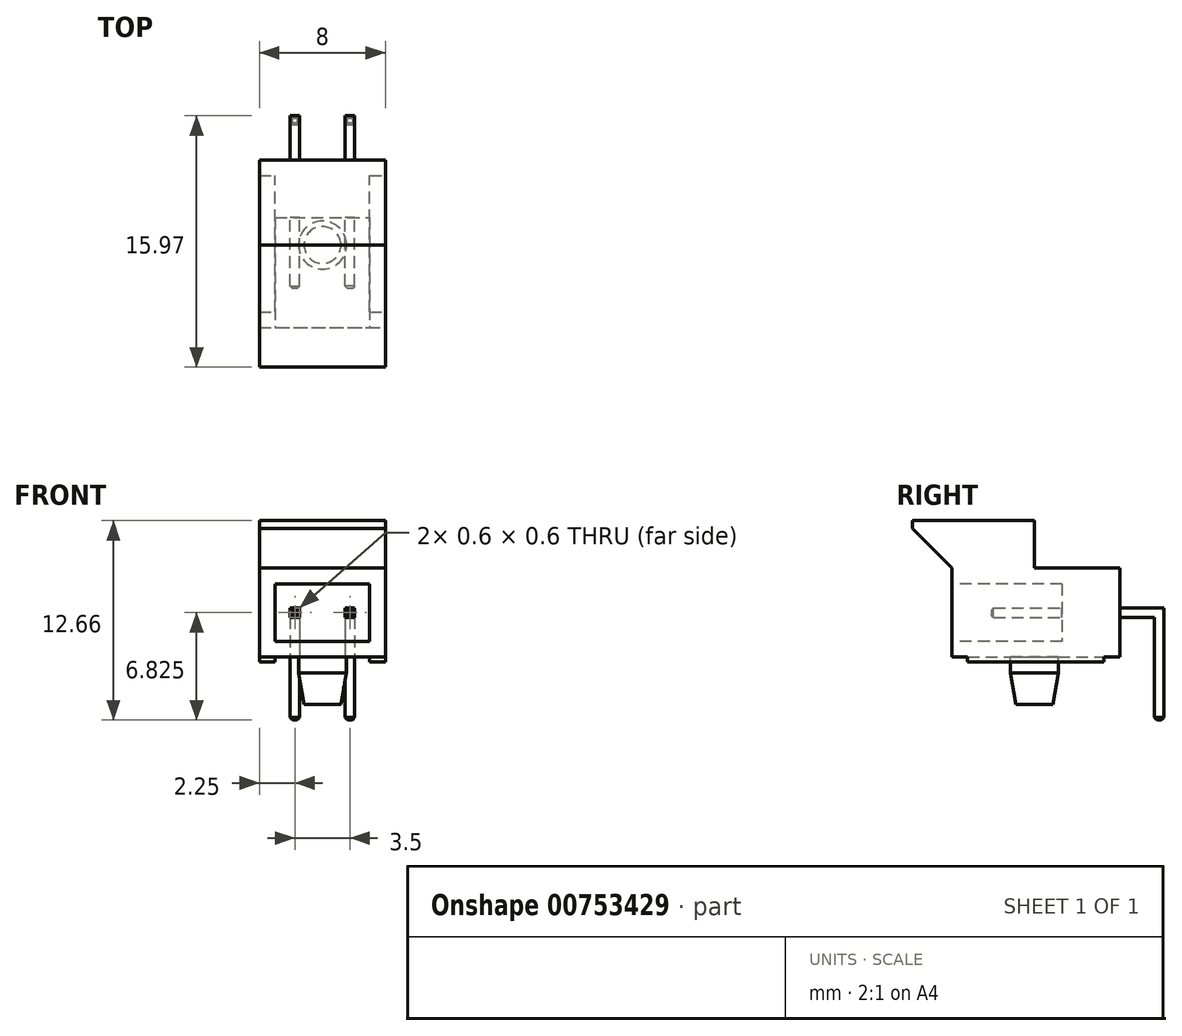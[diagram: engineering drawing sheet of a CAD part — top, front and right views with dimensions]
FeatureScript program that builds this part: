
annotation { "Feature Type Name" : "Feature", "Feature Type Description" : "" }
export const myFeature = defineFeature(function(context is Context, id is Id, definition is map)
    precondition{}
    {
        {
            var Q0;
            Q0=qCreatedBy(makeId("Top.planeOp"),FACE);
            var sketch = newSketch(context, id + "F0", { "sketchPlane" : qUnion([Q0])});
            skLineSegment(sketch, "E0.bottom", {"start": v(-4, 7.83) * mm, "end": v(4, 7.83) * mm});
            skLineSegment(sketch, "E0.top", {"start": v(-4, -7.83) * mm, "end": v(4, -7.83) * mm});
            skLineSegment(sketch, "E0.left", {"start": v(-4, 7.83) * mm, "end": v(-4, -7.83) * mm});
            skLineSegment(sketch, "E0.right", {"start": v(4, 7.83) * mm, "end": v(4, -7.83) * mm});
            skCircle(sketch, "E1", {"center": v(0, -2.58) * mm, "radius": 1.52 * mm});
            skCircle(sketch, "E2", {"center": v(-1.75, 5.33) * mm, "radius": 0.51 * mm});
            skCircle(sketch, "E3", {"center": v(0, 5.33) * mm, "radius": 0.51 * mm, "construction": true});
            skCircle(sketch, "E4", {"center": v(1.75, 5.33) * mm, "radius": 0.51 * mm});
            skLineSegment(sketch, "E5", {"start": v(-4, 2.83) * mm, "end": v(4, 2.83) * mm});
            skSolve(sketch);
        }
        {
            var Q0;
            {var subQ1=sQuery(id+"F0.wireOp",EDGE,"E0.top");Q0=makeQuery(id+"F0.imprint","IMPRINT",FACE,{"disambiguationData":[TD([[makeQuery(id+"F0.imprint","IMPRINT",EDGE,{"derivedFrom":subQ1}),1.0]])]});}
            var Q1;
            Q1=makeQuery(id+"F0.imprint","IMPRINT",FACE,{"disambiguationData":[TD([[makeQuery(id+"F0.imprint","IMPRINT",EDGE,{"derivedFrom":sQuery(id+"F0.wireOp",EDGE,"E1")}),1.0]])]});
            extrude(context, id + "F1", {"entities" : qUnion([Q0, Q1]), "depth" : 5.65 * mm, "offsetDistance" : 25 * mm});
        }
        {
            var Q0;
            Q0=makeQuery(id+"F0.imprint","IMPRINT",FACE,{"disambiguationData":[TD([[makeQuery(id+"F0.imprint","IMPRINT",EDGE,{"derivedFrom":sQuery(id+"F0.wireOp",EDGE,"E1")}),1.0]])]});
            extrude(context, id + "F2", {"entities" : qUnion([Q0]), "operationType" : NewBodyOperationType.ADD, "oppositeDirection" : true, "depth" : 3 * mm, "offsetDistance" : 25 * mm});
        }
        {
            var Q0;
            Q0=makeQuery(id+"F2.opExtrude","CAP_EDGE",EDGE,{"disambiguationData":[OSD([sQuery(id+"F0.wireOp",EDGE,"E1")])],"isStart":false});
            chamfer(context, id + "F3", {"entities" : qUnion([Q0]), "chamferType" : ChamferType.OFFSET_ANGLE, "width" : 2 * mm, "oppositeDirection" : false, "angle" : 10 * degree, "tangentPropagation" : true});
        }
        {
            var Q0;
            Q0=makeQuery(id+"F1.opExtrude","SWEPT_FACE",FACE,{"disambiguationData":[OSD([sQuery(id+"F0.wireOp",EDGE,"E0.top")])]});
            var sketch = newSketch(context, id + "F4", { "sketchPlane" : qUnion([Q0])});
            skLineSegment(sketch, "E6.bottom", {"start": v(-3, 4.65) * mm, "end": v(3, 4.65) * mm});
            skLineSegment(sketch, "E6.top", {"start": v(-3, 1) * mm, "end": v(3, 1) * mm});
            skLineSegment(sketch, "E6.left", {"start": v(-3, 4.65) * mm, "end": v(-3, 1) * mm});
            skLineSegment(sketch, "E6.right", {"start": v(3, 4.65) * mm, "end": v(3, 1) * mm});
            skSolve(sketch);
        }
        {
            var Q0;
            Q0=makeQuery(id+"F4.imprint","IMPRINT",FACE,{"disambiguationData":[TD([[makeQuery(id+"F4.imprint","IMPRINT",EDGE,{"derivedFrom":sQuery(id+"F4.wireOp",EDGE,"E6.bottom")}),-1.0]])]});
            extrude(context, id + "F5", {"entities" : qUnion([Q0]), "operationType" : NewBodyOperationType.REMOVE, "oppositeDirection" : true, "depth" : 7 * mm, "offsetDistance" : 25 * mm});
        }
        {
            var Q0;
            Q0=makeQuery(id+"F1.opExtrude","SWEPT_FACE",FACE,{"disambiguationData":[OSD([sQuery(id+"F0.wireOp",EDGE,"E0.right")])]});
            var Q1;
            Q1=makeQuery(id+"F1.opExtrude","SWEPT_FACE",FACE,{"disambiguationData":[OSD([sQuery(id+"F0.wireOp",EDGE,"E0.left")])]});
            cPlane(context, id + "F6", {"entities" : qUnion([Q0, Q1]), "cplaneType" : CPlaneType.MID_PLANE, "offset" : 25 * mm, "width" : 150 * mm, "height" : 150 * mm});
        }
        {
            var Q0;
            Q0=qCreatedBy(id+"F6.planeOp",FACE);
            var sketch = newSketch(context, id + "F7", { "sketchPlane" : qUnion([Q0])});
            skLineSegment(sketch, "E7.bottom", {"start": v(-5.33, 3.12) * mm, "end": v(5.63, 3.12) * mm});
            skLineSegment(sketch, "E7.top", {"start": v(-5.33, 2.53) * mm, "end": v(5.63, 2.53) * mm});
            skLineSegment(sketch, "E7.left", {"start": v(-5.33, 3.12) * mm, "end": v(-5.33, 2.53) * mm});
            skLineSegment(sketch, "E7.right", {"start": v(5.63, 3.12) * mm, "end": v(5.63, 2.53) * mm});
            skLineSegment(sketch, "E8.bottom", {"start": v(5.63, 3.12) * mm, "end": v(5.03, 3.12) * mm});
            skLineSegment(sketch, "E8.top", {"start": v(5.63, -4) * mm, "end": v(5.03, -4) * mm});
            skLineSegment(sketch, "E8.left", {"start": v(5.63, 3.12) * mm, "end": v(5.63, -4) * mm});
            skLineSegment(sketch, "E8.right", {"start": v(5.03, 3.12) * mm, "end": v(5.03, -4) * mm});
            skLineSegment(sketch, "E9.0", {"start": v(4.82, 0) * mm, "end": v(5.84, 0) * mm});
            skLineSegment(sketch, "E10.0.0", {"start": v(-7.83, 4.65) * mm, "end": v(-7.83, 1) * mm});
            skLineSegment(sketch, "E10.0.1", {"start": v(-7.83, 1) * mm, "end": v(-0.83, 1) * mm});
            skLineSegment(sketch, "E10.0.2", {"start": v(-0.83, 1) * mm, "end": v(-0.83, 4.65) * mm});
            skLineSegment(sketch, "E10.0.3", {"start": v(-0.83, 4.65) * mm, "end": v(-7.83, 4.65) * mm});
            skLineSegment(sketch, "E11", {"start": v(-5.33, 2.83) * mm, "end": v(5.63, 2.83) * mm, "construction": true});
            skLineSegment(sketch, "E12", {"start": v(5.33, 3.12) * mm, "end": v(5.33, -4) * mm, "construction": true});
            skSolve(sketch);
        }
        {
            var Q0;
            Q0=qCreatedBy(id+"F6.planeOp",FACE);
            cPlane(context, id + "F8", {"entities" : qUnion([Q0]), "cplaneType" : CPlaneType.OFFSET, "offset" : 1.75 * mm, "width" : 150 * mm, "height" : 150 * mm});
        }
        {
            var Q0;
            Q0=qCreatedBy(id+"F8.planeOp",FACE);
            var sketch = newSketch(context, id + "F9", { "sketchPlane" : qUnion([Q0])});
            skLineSegment(sketch, "E13.0", {"start": v(-5.33, 3.12) * mm, "end": v(5.63, 3.12) * mm});
            skLineSegment(sketch, "E14.0", {"start": v(-5.33, 2.53) * mm, "end": v(5.63, 2.53) * mm});
            skLineSegment(sketch, "E15.0", {"start": v(-5.33, 3.12) * mm, "end": v(-5.33, 2.53) * mm});
            skLineSegment(sketch, "E16.0", {"start": v(5.63, 3.12) * mm, "end": v(5.63, -4) * mm});
            skLineSegment(sketch, "E17.0", {"start": v(5.03, 3.12) * mm, "end": v(5.03, -4) * mm});
            skLineSegment(sketch, "E18.0", {"start": v(5.63, -4) * mm, "end": v(5.03, -4) * mm});
            skSolve(sketch);
        }
        {
            var Q0;
            Q0=qCreatedBy(id+"F6.planeOp",FACE);
            cPlane(context, id + "F10", {"entities" : qUnion([Q0]), "cplaneType" : CPlaneType.OFFSET, "offset" : 1.75 * mm, "oppositeDirection" : true, "width" : 150 * mm, "height" : 150 * mm});
        }
        {
            var Q0;
            Q0=qCreatedBy(id+"F10.planeOp",FACE);
            var sketch = newSketch(context, id + "F11", { "sketchPlane" : qUnion([Q0])});
            skLineSegment(sketch, "E19.0", {"start": v(-5.33, 3.12) * mm, "end": v(5.63, 3.12) * mm});
            skLineSegment(sketch, "E20.0", {"start": v(5.63, 3.12) * mm, "end": v(5.63, -4) * mm});
            skLineSegment(sketch, "E21.0", {"start": v(5.63, -4) * mm, "end": v(5.03, -4) * mm});
            skLineSegment(sketch, "E22.0", {"start": v(5.03, 3.12) * mm, "end": v(5.03, -4) * mm});
            skLineSegment(sketch, "E23.0", {"start": v(-5.33, 2.53) * mm, "end": v(5.63, 2.53) * mm});
            skLineSegment(sketch, "E24.0", {"start": v(-5.33, 3.12) * mm, "end": v(-5.33, 2.53) * mm});
            skSolve(sketch);
        }
        {
            var Q0;
            Q0=makeQuery(id+"F1.opExtrude","CAP_FACE",FACE,{"disambiguationData":[OSD([sQuery(id+"F0.wireOp",EDGE,"E0.top"),sQuery(id+"F0.wireOp",EDGE,"E0.left"),sQuery(id+"F0.wireOp",EDGE,"E0.right"),sQuery(id+"F0.wireOp",EDGE,"E5")])],"isStart":true});
            var sketch = newSketch(context, id + "F12", { "sketchPlane" : qUnion([Q0])});
            skLineSegment(sketch, "E25.bottom", {"start": v(-4, 6.83) * mm, "end": v(-3, 6.83) * mm});
            skLineSegment(sketch, "E25.top", {"start": v(-4, -1.83) * mm, "end": v(-3, -1.83) * mm});
            skLineSegment(sketch, "E25.left", {"start": v(-4, 6.83) * mm, "end": v(-4, -1.83) * mm});
            skLineSegment(sketch, "E25.right", {"start": v(-3, 6.83) * mm, "end": v(-3, -1.83) * mm});
            skLineSegment(sketch, "E26.bottom", {"start": v(3, 6.83) * mm, "end": v(4, 6.83) * mm});
            skLineSegment(sketch, "E26.top", {"start": v(3, -1.83) * mm, "end": v(4, -1.83) * mm});
            skLineSegment(sketch, "E26.left", {"start": v(3, 6.83) * mm, "end": v(3, -1.83) * mm});
            skLineSegment(sketch, "E26.right", {"start": v(4, 6.83) * mm, "end": v(4, -1.83) * mm});
            skSolve(sketch);
        }
        {
            var Q0;
            Q0=makeQuery(id+"F12.imprint","IMPRINT",FACE,{"disambiguationData":[TD([[makeQuery(id+"F12.imprint","IMPRINT",EDGE,{"derivedFrom":sQuery(id+"F12.wireOp",EDGE,"E26.bottom")}),-1.0]])]});
            var Q1;
            Q1=makeQuery(id+"F12.imprint","IMPRINT",FACE,{"disambiguationData":[TD([[makeQuery(id+"F12.imprint","IMPRINT",EDGE,{"derivedFrom":sQuery(id+"F12.wireOp",EDGE,"E25.bottom")}),-1.0]])]});
            extrude(context, id + "F13", {"entities" : qUnion([Q0, Q1]), "operationType" : NewBodyOperationType.ADD, "depth" : 0.3 * mm, "offsetDistance" : 25 * mm});
        }
        {
            var Q0;
            Q0=makeQuery(id+"F13.boolean.opBoolean","MERGE",FACE,{"derivedFrom":[makeQuery(id+"F1.opExtrude","SWEPT_FACE",FACE,{"disambiguationData":[OSD([sQuery(id+"F0.wireOp",EDGE,"E0.right")])]}),makeQuery(id+"F13.opExtrude","SWEPT_FACE",FACE,{"disambiguationData":[OSD([sQuery(id+"F12.wireOp",EDGE,"E26.right")])]})]});
            var sketch = newSketch(context, id + "F14", { "sketchPlane" : qUnion([Q0])});
            skLineSegment(sketch, "E27", {"start": v(-7.83, 5.65) * mm, "end": v(-10.84, 8.66) * mm});
            skLineSegment(sketch, "E28", {"start": v(-10.84, 8.66) * mm, "end": v(-2.58, 8.66) * mm});
            skLineSegment(sketch, "E29", {"start": v(-2.58, 8.66) * mm, "end": v(-2.58, 5.65) * mm});
            skLineSegment(sketch, "E30.0", {"start": v(-1.4, -3) * mm, "end": v(-3.75, -3) * mm});
            skLineSegment(sketch, "E31", {"start": v(-10.34, 8.16) * mm, "end": v(-10.34, 8.66) * mm});
            skSolve(sketch);
        }
        {
            var Q0;
            {var subQ0=sQuery(id+"F14.wireOp",EDGE,"E29");Q0=makeQuery(id+"F14.imprint","IMPRINT",FACE,{"disambiguationData":[TD([[makeQuery(id+"F14.imprint","IMPRINT",EDGE,{"derivedFrom":subQ0}),-1.0]])]});}
            var Q1;
            Q1=makeQuery(id+"F13.boolean.opBoolean","MERGE",FACE,{"derivedFrom":[makeQuery(id+"F1.opExtrude","SWEPT_FACE",FACE,{"disambiguationData":[OSD([sQuery(id+"F0.wireOp",EDGE,"E0.left")])]}),makeQuery(id+"F13.opExtrude","SWEPT_FACE",FACE,{"disambiguationData":[OSD([sQuery(id+"F12.wireOp",EDGE,"E25.left")])]})]});
            extrude(context, id + "F15", {"entities" : qUnion([Q0]), "operationType" : NewBodyOperationType.ADD, "endBound" : BoundingType.UP_TO_SURFACE, "oppositeDirection" : true, "depth" : 25 * mm, "endBoundEntityFace" : qUnion([Q1]), "offsetDistance" : 25 * mm});
        }
        {
            var Q0;
            {var subQ5=sQuery(id+"F9.wireOp",EDGE,"E18.0");Q0=makeQuery(id+"F9.imprint","IMPRINT",FACE,{"disambiguationData":[TD([[makeQuery(id+"F9.imprint","IMPRINT",EDGE,{"derivedFrom":subQ5}),-1.0]])]});}
            var Q1;
            {var subQ0=sQuery(id+"F9.wireOp",EDGE,"E15.0");Q1=makeQuery(id+"F9.imprint","IMPRINT",FACE,{"disambiguationData":[TD([[makeQuery(id+"F9.imprint","IMPRINT",EDGE,{"derivedFrom":subQ0}),1.0]])]});}
            var Q2;
            {var subQ0=sQuery(id+"F9.wireOp",EDGE,"E16.0");var subQ1=sQuery(id+"F9.wireOp",EDGE,"E13.0");var subQ2=makeQuery(id+"F9.imprint","INTERSECT",VERTEX,{"derivedFrom":[subQ1,subQ0]});Q2=makeQuery(id+"F9.imprint","IMPRINT",FACE,{"disambiguationData":[TD([[makeQuery(id+"F9.imprint","IMPRINT",EDGE,{"disambiguationData":[TD([[subQ2,1.0]])],"derivedFrom":subQ1}),-1.0]])]});}
            var Q3;
            {var subQ0=sQuery(id+"F11.wireOp",EDGE,"E24.0");Q3=makeQuery(id+"F11.imprint","IMPRINT",FACE,{"disambiguationData":[TD([[makeQuery(id+"F11.imprint","IMPRINT",EDGE,{"derivedFrom":subQ0}),1.0]])]});}
            var Q4;
            {var subQ0=sQuery(id+"F11.wireOp",EDGE,"E20.0");var subQ1=sQuery(id+"F11.wireOp",EDGE,"E19.0");var subQ2=makeQuery(id+"F11.imprint","INTERSECT",VERTEX,{"derivedFrom":[subQ1,subQ0]});Q4=makeQuery(id+"F11.imprint","IMPRINT",FACE,{"disambiguationData":[TD([[makeQuery(id+"F11.imprint","IMPRINT",EDGE,{"disambiguationData":[TD([[subQ2,1.0]])],"derivedFrom":subQ1}),-1.0]])]});}
            var Q5;
            {var subQ0=sQuery(id+"F11.wireOp",EDGE,"E21.0");Q5=makeQuery(id+"F11.imprint","IMPRINT",FACE,{"disambiguationData":[TD([[makeQuery(id+"F11.imprint","IMPRINT",EDGE,{"derivedFrom":subQ0}),-1.0]])]});}
            extrude(context, id + "F16", {"entities" : qUnion([Q0, Q1, Q2, Q3, Q4, Q5]), "operationType" : NewBodyOperationType.ADD, "depth" : 0.3 * mm, "offsetDistance" : 25 * mm, "hasSecondDirection" : true, "secondDirectionOppositeDirection" : true, "secondDirectionDepth" : 0.3 * mm});
        }
        {
            var Q0;
            Q0=makeQuery(id+"F16.opExtrude","SWEPT_EDGE",EDGE,{"disambiguationData":[OSD([sQuery(id+"F11.wireOp",EDGE,"E19.0"),sQuery(id+"F11.wireOp",EDGE,"E24.0")])]});
            var Q1;
            Q1=makeQuery(id+"F16.opExtrude","SWEPT_EDGE",EDGE,{"disambiguationData":[OSD([sQuery(id+"F11.wireOp",EDGE,"E23.0"),sQuery(id+"F11.wireOp",EDGE,"E24.0")])]});
            var Q2;
            Q2=makeQuery(id+"F16.opExtrude","CAP_EDGE",EDGE,{"disambiguationData":[OSD([sQuery(id+"F11.wireOp",EDGE,"E24.0")])],"isStart":true});
            var Q3;
            Q3=makeQuery(id+"F16.opExtrude","CAP_EDGE",EDGE,{"disambiguationData":[OSD([sQuery(id+"F11.wireOp",EDGE,"E24.0")])],"isStart":false});
            var Q4;
            Q4=makeQuery(id+"F16.opExtrude","SWEPT_EDGE",EDGE,{"disambiguationData":[OSD([sQuery(id+"F9.wireOp",EDGE,"E13.0"),sQuery(id+"F9.wireOp",EDGE,"E15.0")])]});
            var Q5;
            Q5=makeQuery(id+"F16.opExtrude","CAP_EDGE",EDGE,{"disambiguationData":[OSD([sQuery(id+"F9.wireOp",EDGE,"E15.0")])],"isStart":true});
            var Q6;
            Q6=makeQuery(id+"F16.opExtrude","SWEPT_EDGE",EDGE,{"disambiguationData":[OSD([sQuery(id+"F9.wireOp",EDGE,"E14.0"),sQuery(id+"F9.wireOp",EDGE,"E15.0")])]});
            var Q7;
            Q7=makeQuery(id+"F16.opExtrude","CAP_EDGE",EDGE,{"disambiguationData":[OSD([sQuery(id+"F9.wireOp",EDGE,"E15.0")])],"isStart":false});
            var Q8;
            Q8=makeQuery(id+"F16.opExtrude","SWEPT_EDGE",EDGE,{"disambiguationData":[OSD([sQuery(id+"F9.wireOp",EDGE,"E16.0"),sQuery(id+"F9.wireOp",EDGE,"E18.0")])]});
            var Q9;
            Q9=makeQuery(id+"F16.opExtrude","CAP_EDGE",EDGE,{"disambiguationData":[OSD([sQuery(id+"F9.wireOp",EDGE,"E18.0")])],"isStart":false});
            var Q10;
            Q10=makeQuery(id+"F16.opExtrude","SWEPT_EDGE",EDGE,{"disambiguationData":[OSD([sQuery(id+"F9.wireOp",EDGE,"E17.0"),sQuery(id+"F9.wireOp",EDGE,"E18.0")])]});
            var Q11;
            Q11=makeQuery(id+"F16.opExtrude","CAP_EDGE",EDGE,{"disambiguationData":[OSD([sQuery(id+"F9.wireOp",EDGE,"E18.0")])],"isStart":true});
            var Q12;
            Q12=makeQuery(id+"F16.opExtrude","SWEPT_EDGE",EDGE,{"disambiguationData":[OSD([sQuery(id+"F11.wireOp",EDGE,"E20.0"),sQuery(id+"F11.wireOp",EDGE,"E21.0")])]});
            var Q13;
            Q13=makeQuery(id+"F16.opExtrude","CAP_EDGE",EDGE,{"disambiguationData":[OSD([sQuery(id+"F11.wireOp",EDGE,"E21.0")])],"isStart":false});
            var Q14;
            Q14=makeQuery(id+"F16.opExtrude","SWEPT_EDGE",EDGE,{"disambiguationData":[OSD([sQuery(id+"F11.wireOp",EDGE,"E21.0"),sQuery(id+"F11.wireOp",EDGE,"E22.0")])]});
            var Q15;
            Q15=makeQuery(id+"F16.opExtrude","CAP_EDGE",EDGE,{"disambiguationData":[OSD([sQuery(id+"F11.wireOp",EDGE,"E21.0")])],"isStart":true});
            chamfer(context, id + "F17", {"entities" : qUnion([Q0, Q1, Q2, Q3, Q4, Q5, Q6, Q7, Q8, Q9, Q10, Q11, Q12, Q13, Q14, Q15]), "width" : 0.15 * mm, "tangentPropagation" : true});
        }
    });
